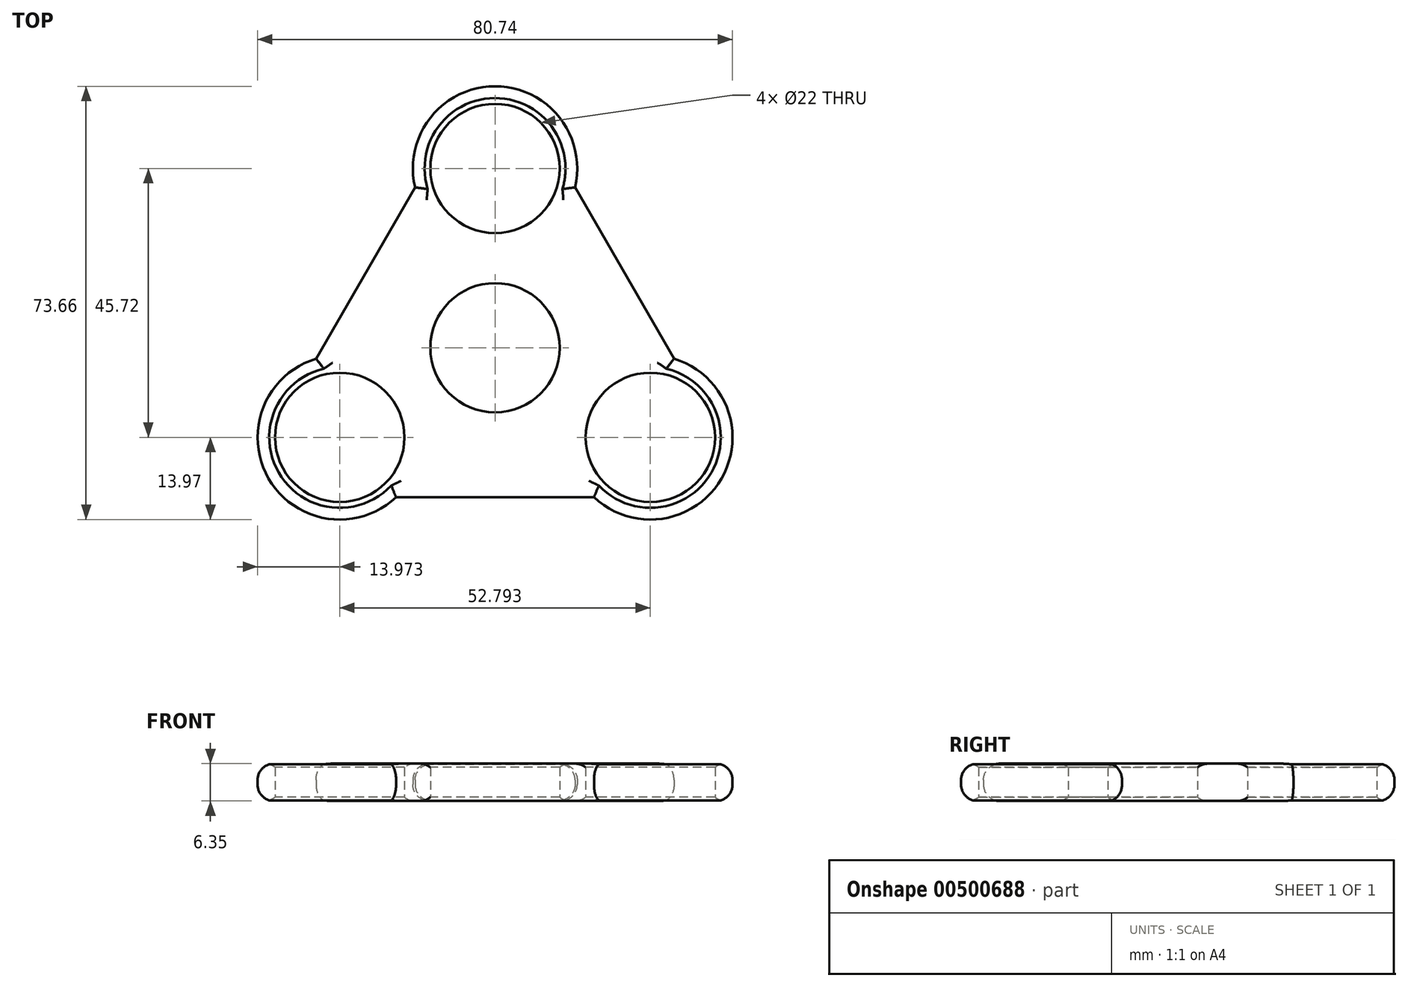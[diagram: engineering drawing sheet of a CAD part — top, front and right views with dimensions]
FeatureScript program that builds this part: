
annotation { "Feature Type Name" : "Feature", "Feature Type Description" : "" }
export const myFeature = defineFeature(function(context is Context, id is Id, definition is map)
    precondition{}
    {
        {
            var Q0;
            Q0=qCreatedBy(makeId("Top.planeOp"),FACE);
            var sketch = newSketch(context, id + "F0", { "sketchPlane" : qUnion([Q0])});
            skCircle(sketch, "E0", {"center": v(0, 0) * mm, "radius": 44.45 * mm});
            skCircle(sketch, "E1", {"center": v(0, 0) * mm, "radius": 11 * mm});
            skCircle(sketch, "E2", {"center": v(0, 30.48) * mm, "radius": 11 * mm});
            skCircle(sketch, "E3.1.0", {"center": v(-26.4, -15.24) * mm, "radius": 11 * mm});
            skCircle(sketch, "E3.2.0", {"center": v(26.4, -15.24) * mm, "radius": 11 * mm});
            skCircle(sketch, "E4", {"center": v(0, 30.48) * mm, "radius": 13.97 * mm});
            skCircle(sketch, "E5", {"center": v(-26.4, -15.24) * mm, "radius": 13.97 * mm});
            skCircle(sketch, "E6", {"center": v(26.4, -15.24) * mm, "radius": 13.97 * mm});
            skCircle(sketch, "E7", {"center": v(0, 0) * mm, "radius": 13.97 * mm});
            skCircle(sketch, "E8.cCircle", {"center": v(0, 0) * mm, "radius": 30.48 * mm, "construction": true});
            skLineSegment(sketch, "E8.0", {"start": v(6.99, 18.38) * mm, "end": v(19.41, -3.14) * mm});
            skLineSegment(sketch, "E8.1", {"start": v(12.43, -15.24) * mm, "end": v(-12.43, -15.24) * mm});
            skLineSegment(sketch, "E8.2", {"start": v(-19.41, -3.14) * mm, "end": v(-6.98, 18.38) * mm});
            skLineSegment(sketch, "E9", {"start": v(13.6, 27.28) * mm, "end": v(30.42, -1.86) * mm});
            skLineSegment(sketch, "E10.1.0", {"start": v(-30.42, -1.86) * mm, "end": v(-13.6, 27.28) * mm});
            skLineSegment(sketch, "E10.2.0", {"start": v(16.82, -25.42) * mm, "end": v(-16.82, -25.42) * mm});
            skSolve(sketch);
        }
        {
            var Q0;
            Q0=makeQuery(id+"F0.imprint","IMPRINT",FACE,{"disambiguationData":[TD([[makeQuery(id+"F0.imprint","IMPRINT",EDGE,{"derivedFrom":sQuery(id+"F0.wireOp",EDGE,"E2")}),-1.0]])]});
            var Q1;
            Q1=makeQuery(id+"F0.imprint","IMPRINT",FACE,{"disambiguationData":[TD([[makeQuery(id+"F0.imprint","IMPRINT",EDGE,{"derivedFrom":sQuery(id+"F0.wireOp",EDGE,"E3.2.0")}),-1.0]])]});
            var Q2;
            Q2=makeQuery(id+"F0.imprint","IMPRINT",FACE,{"disambiguationData":[TD([[makeQuery(id+"F0.imprint","IMPRINT",EDGE,{"derivedFrom":sQuery(id+"F0.wireOp",EDGE,"E3.1.0")}),-1.0]])]});
            var Q3;
            Q3=makeQuery(id+"F0.imprint","IMPRINT",FACE,{"disambiguationData":[TD([[makeQuery(id+"F0.imprint","IMPRINT",EDGE,{"derivedFrom":sQuery(id+"F0.wireOp",EDGE,"E7")}),-1.0]])]});
            var Q4;
            Q4=makeQuery(id+"F0.imprint","IMPRINT",FACE,{"disambiguationData":[TD([[makeQuery(id+"F0.imprint","IMPRINT",EDGE,{"derivedFrom":sQuery(id+"F0.wireOp",EDGE,"E1")}),-1.0]])]});
            extrude(context, id + "F1", {"entities" : qUnion([Q0, Q1, Q2, Q3, Q4]), "depth" : 6.35 * mm});
        }
        {
            var Q0;
            Q0=makeQuery(id+"F1.opExtrude","CAP_EDGE",EDGE,{"disambiguationData":[OSD([sQuery(id+"F0.wireOp",EDGE,"E1")])],"isStart":false});
            var Q1;
            Q1=makeQuery(id+"F1.opExtrude","CAP_EDGE",EDGE,{"disambiguationData":[OSD([sQuery(id+"F0.wireOp",EDGE,"E1")])],"isStart":true});
            var Q2;
            Q2=makeQuery(id+"F1.opExtrude","CAP_EDGE",EDGE,{"disambiguationData":[OSD([sQuery(id+"F0.wireOp",EDGE,"E2")])],"isStart":false});
            var Q3;
            Q3=makeQuery(id+"F1.opExtrude","CAP_EDGE",EDGE,{"disambiguationData":[OSD([sQuery(id+"F0.wireOp",EDGE,"E3.2.0")])],"isStart":false});
            var Q4;
            Q4=makeQuery(id+"F1.opExtrude","CAP_EDGE",EDGE,{"disambiguationData":[OSD([sQuery(id+"F0.wireOp",EDGE,"E3.1.0")])],"isStart":false});
            var Q5;
            Q5=makeQuery(id+"F1.opExtrude","CAP_EDGE",EDGE,{"disambiguationData":[OSD([sQuery(id+"F0.wireOp",EDGE,"E2")])],"isStart":true});
            var Q6;
            Q6=makeQuery(id+"F1.opExtrude","CAP_EDGE",EDGE,{"disambiguationData":[OSD([sQuery(id+"F0.wireOp",EDGE,"E3.2.0")])],"isStart":true});
            var Q7;
            Q7=makeQuery(id+"F1.opExtrude","CAP_EDGE",EDGE,{"disambiguationData":[OSD([sQuery(id+"F0.wireOp",EDGE,"E3.1.0")])],"isStart":true});
            chamfer(context, id + "F2", {"entities" : qUnion([Q0, Q1, Q2, Q3, Q4, Q5, Q6, Q7]), "width" : 0.64 * mm, "tangentPropagation" : true});
        }
        {
            var Q0;
            {var subQ0=sQuery(id+"F0.wireOp",EDGE,"E8.2");Q0=makeQuery(id+"F0.imprint","IMPRINT",FACE,{"disambiguationData":[TD([[makeQuery(id+"F0.imprint","IMPRINT",EDGE,{"derivedFrom":subQ0}),1.0]])]});}
            var Q1;
            {var subQ0=sQuery(id+"F0.wireOp",EDGE,"E8.0");Q1=makeQuery(id+"F0.imprint","IMPRINT",FACE,{"disambiguationData":[TD([[makeQuery(id+"F0.imprint","IMPRINT",EDGE,{"derivedFrom":subQ0}),1.0]])]});}
            var Q2;
            {var subQ0=sQuery(id+"F0.wireOp",EDGE,"E8.1");Q2=makeQuery(id+"F0.imprint","IMPRINT",FACE,{"disambiguationData":[TD([[makeQuery(id+"F0.imprint","IMPRINT",EDGE,{"derivedFrom":subQ0}),1.0]])]});}
            extrude(context, id + "F3", {"entities" : qUnion([Q0, Q1, Q2]), "operationType" : NewBodyOperationType.ADD, "depth" : 6.35 * mm});
        }
        {
            var Q0;
            {var subQ0=sQuery(id+"F0.wireOp",EDGE,"E8.1");var subQ1=sQuery(id+"F0.wireOp",EDGE,"E6");var subQ2=sQuery(id+"F0.wireOp",EDGE,"E5");var subQ3=sQuery(id+"F0.wireOp",EDGE,"E8.0");var subQ4=sQuery(id+"F0.wireOp",EDGE,"E4");var subQ5=sQuery(id+"F0.wireOp",EDGE,"E8.2");Q0=makeQuery(id+"F3.boolean.opBoolean","MERGE",FACE,{"derivedFrom":[makeQuery(id+"F1.opExtrude","CAP_FACE",FACE,{"disambiguationData":[OSD([sQuery(id+"F0.wireOp",EDGE,"E1"),sQuery(id+"F0.wireOp",EDGE,"E2"),sQuery(id+"F0.wireOp",EDGE,"E3.1.0"),sQuery(id+"F0.wireOp",EDGE,"E3.2.0"),subQ4,subQ2,subQ1,subQ3,subQ0,subQ5])],"isStart":false}),makeQuery(id+"F3.opExtrude","CAP_FACE",FACE,{"disambiguationData":[OSD([subQ4,subQ2,subQ5,sQuery(id+"F0.wireOp",EDGE,"E10.1.0")])],"isStart":false}),makeQuery(id+"F3.opExtrude","CAP_FACE",FACE,{"disambiguationData":[OSD([subQ4,subQ1,subQ3,sQuery(id+"F0.wireOp",EDGE,"E9")])],"isStart":false}),makeQuery(id+"F3.opExtrude","CAP_FACE",FACE,{"disambiguationData":[OSD([subQ2,subQ1,subQ0,sQuery(id+"F0.wireOp",EDGE,"E10.2.0")])],"isStart":false})]});}
            var Q1;
            {var subQ0=sQuery(id+"F0.wireOp",EDGE,"E1");Q1=makeQuery(id+"F2.opChamfer","BLEND_EDGE",EDGE,{"blendedFrom":[makeQuery(id+"F1.opExtrude","CAP_EDGE",EDGE,{"disambiguationData":[OSD([subQ0])],"isStart":true}),makeQuery(id+"F1.opExtrude","CAP_FACE",FACE,{"disambiguationData":[OSD([subQ0,sQuery(id+"F0.wireOp",EDGE,"E2"),sQuery(id+"F0.wireOp",EDGE,"E3.1.0"),sQuery(id+"F0.wireOp",EDGE,"E3.2.0"),sQuery(id+"F0.wireOp",EDGE,"E4"),sQuery(id+"F0.wireOp",EDGE,"E5"),sQuery(id+"F0.wireOp",EDGE,"E6"),sQuery(id+"F0.wireOp",EDGE,"E8.0"),sQuery(id+"F0.wireOp",EDGE,"E8.1"),sQuery(id+"F0.wireOp",EDGE,"E8.2")])],"isStart":true})],"blendedInto":[makeQuery(id+"F1.opExtrude","CAP_FACE",FACE,{"disambiguationData":[OSD([subQ0,sQuery(id+"F0.wireOp",EDGE,"E2"),sQuery(id+"F0.wireOp",EDGE,"E3.1.0"),sQuery(id+"F0.wireOp",EDGE,"E3.2.0"),sQuery(id+"F0.wireOp",EDGE,"E4"),sQuery(id+"F0.wireOp",EDGE,"E5"),sQuery(id+"F0.wireOp",EDGE,"E6"),sQuery(id+"F0.wireOp",EDGE,"E8.0"),sQuery(id+"F0.wireOp",EDGE,"E8.1"),sQuery(id+"F0.wireOp",EDGE,"E8.2")])],"isStart":true})]});}
            var Q2;
            {var subQ0=sQuery(id+"F0.wireOp",EDGE,"E8.1");var subQ1=sQuery(id+"F0.wireOp",EDGE,"E6");var subQ2=sQuery(id+"F0.wireOp",EDGE,"E5");var subQ3=sQuery(id+"F0.wireOp",EDGE,"E8.0");var subQ4=sQuery(id+"F0.wireOp",EDGE,"E4");var subQ5=sQuery(id+"F0.wireOp",EDGE,"E8.2");Q2=makeQuery(id+"F3.boolean.opBoolean","MERGE",FACE,{"derivedFrom":[makeQuery(id+"F1.opExtrude","CAP_FACE",FACE,{"disambiguationData":[OSD([sQuery(id+"F0.wireOp",EDGE,"E1"),sQuery(id+"F0.wireOp",EDGE,"E2"),sQuery(id+"F0.wireOp",EDGE,"E3.1.0"),sQuery(id+"F0.wireOp",EDGE,"E3.2.0"),subQ4,subQ2,subQ1,subQ3,subQ0,subQ5])],"isStart":true}),makeQuery(id+"F3.opExtrude","CAP_FACE",FACE,{"disambiguationData":[OSD([subQ4,subQ2,subQ5,sQuery(id+"F0.wireOp",EDGE,"E10.1.0")])],"isStart":true}),makeQuery(id+"F3.opExtrude","CAP_FACE",FACE,{"disambiguationData":[OSD([subQ4,subQ1,subQ3,sQuery(id+"F0.wireOp",EDGE,"E9")])],"isStart":true}),makeQuery(id+"F3.opExtrude","CAP_FACE",FACE,{"disambiguationData":[OSD([subQ2,subQ1,subQ0,sQuery(id+"F0.wireOp",EDGE,"E10.2.0")])],"isStart":true})]});}
            fillet(context, id + "F4", {"entities" : qUnion([Q0, Q1, Q2]), "radius" : 2.8 * mm, "tangentPropagation" : true, "allowEdgeOverflow" : false});
        }
    });
